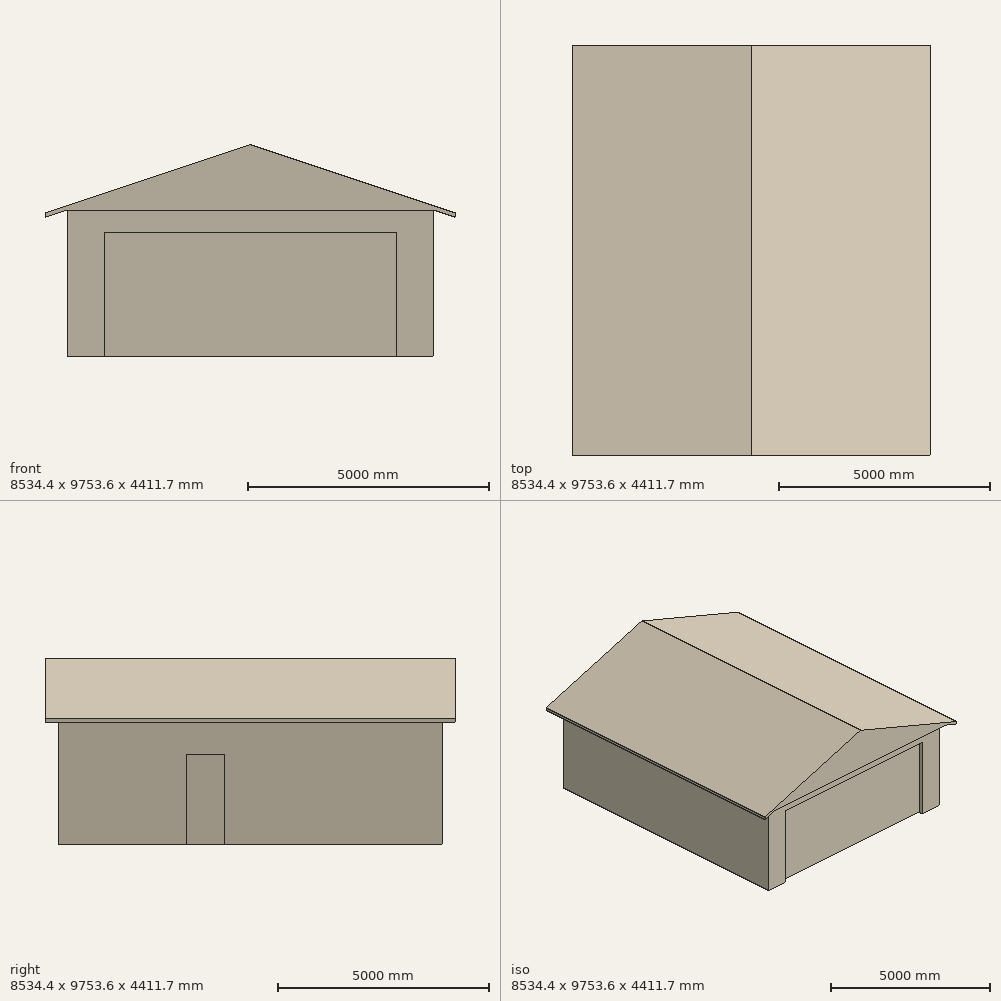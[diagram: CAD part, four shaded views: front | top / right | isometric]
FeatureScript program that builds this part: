
annotation { "Feature Type Name" : "Feature", "Feature Type Description" : "" }
export const myFeature = defineFeature(function(context is Context, id is Id, definition is map)
    precondition{}
    {
        {
            var Q0;
            Q0=qCreatedBy(makeId("Top.planeOp"),FACE);
            var sketch = newSketch(context, id + "F0", { "sketchPlane" : qUnion([Q0])});
            skLineSegment(sketch, "E0.bottom", {"start": v(0, 0) * mm, "end": v(7620, 0) * mm});
            skLineSegment(sketch, "E0.top", {"start": v(0, 9144) * mm, "end": v(7620, 9144) * mm});
            skLineSegment(sketch, "E0.left", {"start": v(0, 0) * mm, "end": v(0, 9144) * mm});
            skLineSegment(sketch, "E0.right", {"start": v(7620, 0) * mm, "end": v(7620, 9144) * mm});
            skSolve(sketch);
        }
        {
            var Q0;
            Q0 = qSketchRegion(id + "F0", true);
            extrude(context, id + "F1", {"entities" : qUnion([Q0]), "depth" : 3048 * mm, "offsetDistance" : 25.4 * mm});
        }
        {
            var Q0;
            Q0=makeQuery(id+"F1.opExtrude","SWEPT_FACE",FACE,{"disambiguationData":[OSD([sQuery(id+"F0.wireOp",EDGE,"E0.bottom")])]});
            var sketch = newSketch(context, id + "F2", { "sketchPlane" : qUnion([Q0])});
            skLineSegment(sketch, "E1", {"start": v(-457.2, 2989.3) * mm, "end": v(-457.2, 2895.6) * mm});
            skLineSegment(sketch, "E2", {"start": v(-457.2, 2895.6) * mm, "end": v(3810, 4318) * mm});
            skLineSegment(sketch, "E3", {"start": v(3810, 4318) * mm, "end": v(8077.2, 2895.6) * mm});
            skLineSegment(sketch, "E4", {"start": v(8077.2, 2895.6) * mm, "end": v(8077.2, 2989.3) * mm});
            skLineSegment(sketch, "E5", {"start": v(8077.2, 2989.3) * mm, "end": v(3810, 4411.7) * mm});
            skLineSegment(sketch, "E6", {"start": v(3810, 4411.7) * mm, "end": v(-457.2, 2989.3) * mm});
            skLineSegment(sketch, "E7", {"start": v(3810, 4318) * mm, "end": v(3810, 3048) * mm, "construction": true});
            skLineSegment(sketch, "E8", {"start": v(2111.34, 3751.78) * mm, "end": v(2416.14, 3751.78) * mm, "construction": true});
            skLineSegment(sketch, "E9", {"start": v(2416.14, 3751.78) * mm, "end": v(2416.14, 3853.38) * mm, "construction": true});
            skLineSegment(sketch, "E10", {"start": v(7620, 3048) * mm, "end": v(0, 3048) * mm});
            skSolve(sketch);
        }
        {
            var Q0;
            Q0 = qSketchRegion(id + "F2", true);
            extrude(context, id + "F3", {"entities" : qUnion([Q0]), "operationType" : NewBodyOperationType.ADD, "depth" : 304.8 * mm, "offsetDistance" : 25.4 * mm, "hasSecondDirection" : true, "secondDirectionOppositeDirection" : true, "secondDirectionDepth" : 9448.8 * mm});
        }
        {
            var Q0;
            Q0=makeQuery(id+"F1.opExtrude","SWEPT_FACE",FACE,{"disambiguationData":[OSD([sQuery(id+"F0.wireOp",EDGE,"E0.bottom")])]});
            var sketch = newSketch(context, id + "F4", { "sketchPlane" : qUnion([Q0])});
            skLineSegment(sketch, "E11.bottom", {"start": v(762, 0) * mm, "end": v(6858, 0) * mm});
            skLineSegment(sketch, "E11.top", {"start": v(762, 2590.8) * mm, "end": v(6858, 2590.8) * mm});
            skLineSegment(sketch, "E11.left", {"start": v(762, 0) * mm, "end": v(762, 2590.8) * mm});
            skLineSegment(sketch, "E11.right", {"start": v(6858, 0) * mm, "end": v(6858, 2590.8) * mm});
            skLineSegment(sketch, "E12", {"start": v(3810, 0) * mm, "end": v(3810, 2590.8) * mm, "construction": true});
            skSolve(sketch);
        }
        {
            var Q0;
            Q0 = qSketchRegion(id + "F4", true);
            extrude(context, id + "F5", {"entities" : qUnion([Q0]), "operationType" : NewBodyOperationType.REMOVE, "oppositeDirection" : true, "depth" : 139.7 * mm, "offsetDistance" : 25.4 * mm});
        }
        {
            var Q0;
            Q0=makeQuery(id+"F1.opExtrude","SWEPT_FACE",FACE,{"disambiguationData":[OSD([sQuery(id+"F0.wireOp",EDGE,"E0.right")])]});
            var sketch = newSketch(context, id + "F6", { "sketchPlane" : qUnion([Q0])});
            skLineSegment(sketch, "E13.bottom", {"start": v(3048, 0) * mm, "end": v(3962.4, 0) * mm});
            skLineSegment(sketch, "E13.top", {"start": v(3048, 2133.6) * mm, "end": v(3962.4, 2133.6) * mm});
            skLineSegment(sketch, "E13.left", {"start": v(3048, 0) * mm, "end": v(3048, 2133.6) * mm});
            skLineSegment(sketch, "E13.right", {"start": v(3962.4, 0) * mm, "end": v(3962.4, 2133.6) * mm});
            skSolve(sketch);
        }
        {
            var Q0;
            Q0 = qSketchRegion(id + "F6", true);
            extrude(context, id + "F7", {"entities" : qUnion([Q0]), "operationType" : NewBodyOperationType.REMOVE, "oppositeDirection" : true, "depth" : 139.7 * mm, "offsetDistance" : 25.4 * mm});
        }
    });
